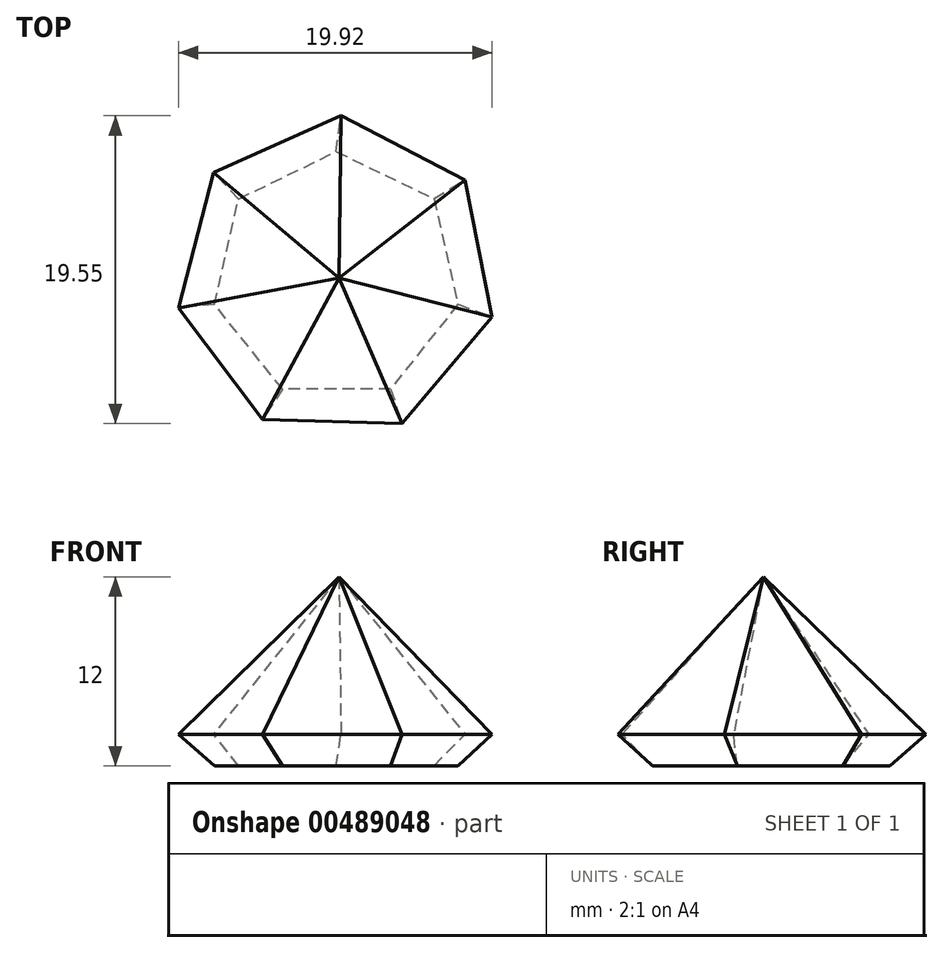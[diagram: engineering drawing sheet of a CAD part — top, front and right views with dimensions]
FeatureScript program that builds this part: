
annotation { "Feature Type Name" : "Feature", "Feature Type Description" : "" }
export const myFeature = defineFeature(function(context is Context, id is Id, definition is map)
    precondition{}
    {
        {
            var Q0;
            Q0=qCreatedBy(makeId("Top.planeOp"),FACE);
            var sketch = newSketch(context, id + "F0", { "sketchPlane" : qUnion([Q0])});
            skCircle(sketch, "E0.cCircle", {"center": v(0, 0) * mm, "radius": 7.14 * mm, "construction": true});
            skLineSegment(sketch, "E0.0", {"start": v(6.2, 4.95) * mm, "end": v(7.73, -1.75) * mm});
            skLineSegment(sketch, "E0.1", {"start": v(7.73, -1.75) * mm, "end": v(3.45, -7.14) * mm});
            skLineSegment(sketch, "E0.2", {"start": v(3.45, -7.14) * mm, "end": v(-3.43, -7.15) * mm});
            skLineSegment(sketch, "E0.3", {"start": v(-3.43, -7.15) * mm, "end": v(-7.73, -1.78) * mm});
            skLineSegment(sketch, "E0.4", {"start": v(-7.73, -1.78) * mm, "end": v(-6.2, 4.93) * mm});
            skLineSegment(sketch, "E0.5", {"start": v(-6.2, 4.93) * mm, "end": v(-0.01, 7.93) * mm});
            skLineSegment(sketch, "E0.6", {"start": v(-0.01, 7.93) * mm, "end": v(6.2, 4.95) * mm});
            skPoint(sketch, "E0.0.midPoint", {"position": v(6.96, 1.6) * mm});
            skSolve(sketch);
        }
        {
            var Q0;
            Q0=qCreatedBy(makeId("Top.planeOp"),FACE);
            cPlane(context, id + "F1", {"entities" : qUnion([Q0]), "cplaneType" : CPlaneType.OFFSET, "offset" : 2 * mm, "width" : 150 * mm, "height" : 150 * mm});
        }
        {
            var Q0;
            Q0=qCreatedBy(id+"F1.planeOp",FACE);
            var sketch = newSketch(context, id + "F2", { "sketchPlane" : qUnion([Q0])});
            skCircle(sketch, "E1.cCircle", {"center": v(0, 0) * mm, "radius": 9.2 * mm, "construction": true});
            skLineSegment(sketch, "E1.0", {"start": v(8.17, 6.14) * mm, "end": v(9.9, -2.56) * mm});
            skLineSegment(sketch, "E1.1", {"start": v(9.9, -2.56) * mm, "end": v(4.17, -9.33) * mm});
            skLineSegment(sketch, "E1.2", {"start": v(4.17, -9.33) * mm, "end": v(-4.7, -9.07) * mm});
            skLineSegment(sketch, "E1.3", {"start": v(-4.7, -9.07) * mm, "end": v(-10.03, -1.98) * mm});
            skLineSegment(sketch, "E1.4", {"start": v(-10.03, -1.98) * mm, "end": v(-7.8, 6.6) * mm});
            skLineSegment(sketch, "E1.5", {"start": v(-7.8, 6.6) * mm, "end": v(0.3, 10.22) * mm});
            skLineSegment(sketch, "E1.6", {"start": v(0.3, 10.22) * mm, "end": v(8.17, 6.14) * mm});
            skPoint(sketch, "E1.0.midPoint", {"position": v(9.03, 1.79) * mm});
            skSolve(sketch);
        }
        {
            var Q0;
            Q0=qCreatedBy(id+"F1.planeOp",FACE);
            cPlane(context, id + "F3", {"entities" : qUnion([Q0]), "cplaneType" : CPlaneType.OFFSET, "offset" : 10 * mm, "width" : 150 * mm, "height" : 150 * mm});
        }
        {
            var Q0;
            Q0=qCreatedBy(id+"F3.planeOp",FACE);
            var sketch = newSketch(context, id + "F4", { "sketchPlane" : qUnion([Q0])});
            skCircle(sketch, "E2.cCircle", {"center": v(0, 0) * mm, "radius": 0.2 * mm, "construction": true});
            skLineSegment(sketch, "E2.0", {"start": v(0.22, -0.02) * mm, "end": v(0.12, -0.19) * mm});
            skLineSegment(sketch, "E2.1", {"start": v(0.12, -0.19) * mm, "end": v(-0.07, -0.21) * mm});
            skLineSegment(sketch, "E2.2", {"start": v(-0.07, -0.21) * mm, "end": v(-0.2, -0.08) * mm});
            skLineSegment(sketch, "E2.3", {"start": v(-0.2, -0.08) * mm, "end": v(-0.2, 0.11) * mm});
            skLineSegment(sketch, "E2.4", {"start": v(-0.2, 0.11) * mm, "end": v(-0.03, 0.22) * mm});
            skLineSegment(sketch, "E2.5", {"start": v(-0.03, 0.22) * mm, "end": v(0.15, 0.16) * mm});
            skLineSegment(sketch, "E2.6", {"start": v(0.15, 0.16) * mm, "end": v(0.22, -0.02) * mm});
            skPoint(sketch, "E2.0.midPoint", {"position": v(0.17, -0.1) * mm});
            skSolve(sketch);
        }
        {
            var Q0;
            Q0=sQuery(id+"F4.wireOp",VERTEX,"E2.0.midPoint");
            var Q1;
            Q1=makeQuery(id+"F2.imprint","IMPRINT",FACE,{"disambiguationData":[TD([[makeQuery(id+"F2.imprint","IMPRINT",EDGE,{"derivedFrom":sQuery(id+"F2.wireOp",EDGE,"E1.0")}),-1.0]])]});
            loft(context, id + "F5", {"sheetProfilesArray" : [{ "sheetProfileEntities" : qUnion([Q0]) }, { "sheetProfileEntities" : qUnion([Q1]) }]});
        }
        {
            var Q1;
            Q1=makeQuery(id+"F0.imprint","IMPRINT",FACE,{"disambiguationData":[TD([[makeQuery(id+"F0.imprint","IMPRINT",EDGE,{"derivedFrom":sQuery(id+"F0.wireOp",EDGE,"E0.0")}),-1.0]])]});
            var Q2;
            Q2=makeQuery(id+"F5.opLoft","CAP_FACE",FACE,{"disambiguationData":[OSD([makeQuery(id+"F2.imprint","IMPRINT",FACE,{"disambiguationData":[TD([[makeQuery(id+"F2.imprint","IMPRINT",EDGE,{"derivedFrom":sQuery(id+"F2.wireOp",EDGE,"E1.0")}),-1.0]])]})])],"isStart":true});
            loft(context, id + "F6", {"operationType" : NewBodyOperationType.ADD, "sheetProfilesArray" : [{ "sheetProfileEntities" : qUnion([Q1]) }, { "sheetProfileEntities" : qUnion([Q2]) }]});
        }
    });
